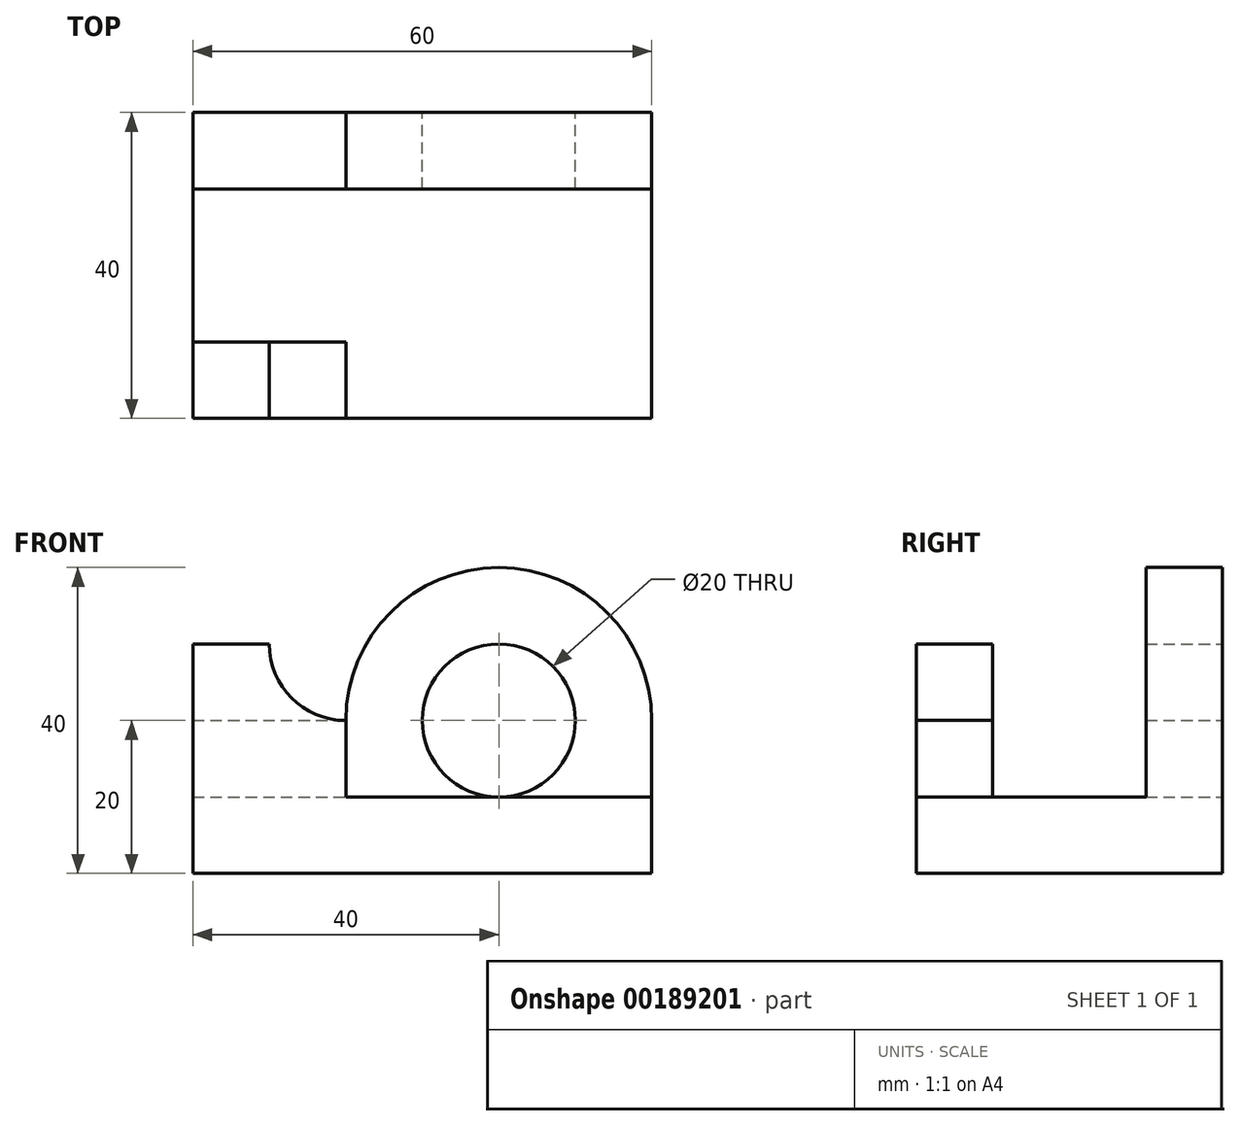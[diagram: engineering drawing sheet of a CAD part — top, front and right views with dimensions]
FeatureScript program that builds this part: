
annotation { "Feature Type Name" : "Feature", "Feature Type Description" : "" }
export const myFeature = defineFeature(function(context is Context, id is Id, definition is map)
    precondition{}
    {
        {
            var Q0;
            Q0=qCreatedBy(makeId("Top.planeOp"),FACE);
            var sketch = newSketch(context, id + "F0", { "sketchPlane" : qUnion([Q0])});
            skLineSegment(sketch, "E0.bottom", {"start": v(0, 0) * mm, "end": v(60, 0) * mm});
            skLineSegment(sketch, "E0.top", {"start": v(0, 40) * mm, "end": v(60, 40) * mm});
            skLineSegment(sketch, "E0.left", {"start": v(0, 0) * mm, "end": v(0, 40) * mm});
            skLineSegment(sketch, "E0.right", {"start": v(60, 0) * mm, "end": v(60, 40) * mm});
            skSolve(sketch);
        }
        {
            var Q0;
            Q0=makeQuery(id+"F0.imprint","IMPRINT",FACE,{"disambiguationData":[TD([[makeQuery(id+"F0.imprint","IMPRINT",EDGE,{"derivedFrom":sQuery(id+"F0.wireOp",EDGE,"E0.bottom")}),1.0]])]});
            extrude(context, id + "F1", {"entities" : qUnion([Q0]), "depth" : 10 * mm});
        }
        {
            var Q0;
            Q0=makeQuery(id+"F1.opExtrude","SWEPT_FACE",FACE,{"disambiguationData":[OSD([sQuery(id+"F0.wireOp",EDGE,"E0.bottom")])]});
            var sketch = newSketch(context, id + "F2", { "sketchPlane" : qUnion([Q0])});
            skLineSegment(sketch, "E1", {"start": v(0, 10) * mm, "end": v(0, 30) * mm});
            skLineSegment(sketch, "E2", {"start": v(0, 30) * mm, "end": v(10, 30) * mm});
            skLineSegment(sketch, "E3", {"start": v(0, 10) * mm, "end": v(20, 10) * mm});
            skLineSegment(sketch, "E4", {"start": v(20, 10) * mm, "end": v(20, 20) * mm});
            skArc(sketch, "E5", {"start": v(10, 30) * mm, "mid": v(12.93, 22.93) * mm, "end": v(20, 20) * mm});
            skSolve(sketch);
        }
        {
            var Q0;
            Q0=makeQuery(id+"F2.imprint","IMPRINT",FACE,{"disambiguationData":[TD([[makeQuery(id+"F2.imprint","IMPRINT",EDGE,{"derivedFrom":sQuery(id+"F2.wireOp",EDGE,"E1")}),-1.0]])]});
            extrude(context, id + "F3", {"entities" : qUnion([Q0]), "operationType" : NewBodyOperationType.ADD, "oppositeDirection" : true, "depth" : 10 * mm});
        }
        {
            var Q0;
            Q0=makeQuery(id+"F1.opExtrude","SWEPT_FACE",FACE,{"disambiguationData":[OSD([sQuery(id+"F0.wireOp",EDGE,"E0.top")])]});
            var sketch = newSketch(context, id + "F4", { "sketchPlane" : qUnion([Q0])});
            skLineSegment(sketch, "E6.0", {"start": v(0, 10) * mm, "end": v(-60, 10) * mm});
            skLineSegment(sketch, "E7", {"start": v(-60, 10) * mm, "end": v(-60, 20) * mm});
            skLineSegment(sketch, "E8", {"start": v(0, 10) * mm, "end": v(0, 20) * mm});
            skArc(sketch, "E9", {"start": v(-20, 20) * mm, "mid": v(-40, 40) * mm, "end": v(-60, 20) * mm});
            skLineSegment(sketch, "E10", {"start": v(0, 20) * mm, "end": v(-20, 20) * mm});
            skSolve(sketch);
        }
        {
            var Q0;
            {var subQ1=sQuery(id+"F4.wireOp",EDGE,"E7");Q0=makeQuery(id+"F4.imprint","IMPRINT",FACE,{"disambiguationData":[TD([[makeQuery(id+"F4.imprint","IMPRINT",EDGE,{"derivedFrom":subQ1}),-1.0]])]});}
            extrude(context, id + "F5", {"entities" : qUnion([Q0]), "operationType" : NewBodyOperationType.ADD, "oppositeDirection" : true, "depth" : 10 * mm});
        }
        {
            var Q0;
            Q0=makeQuery(id+"F4.imprint","IMPRINT",FACE,{"disambiguationData":[TD([[makeQuery(id+"F4.imprint","IMPRINT",EDGE,{"derivedFrom":sQuery(id+"F4.wireOp",EDGE,"E6.0")}),-1.0]])]});
            var sketch = newSketch(context, id + "F6", { "sketchPlane" : qUnion([Q0])});
            skCircle(sketch, "E11", {"center": v(-40, 20) * mm, "radius": 10 * mm});
            skSolve(sketch);
        }
        {
            var Q0;
            Q0=makeQuery(id+"F6.imprint","IMPRINT",FACE,{"disambiguationData":[TD([[makeQuery(id+"F6.imprint","IMPRINT",EDGE,{"derivedFrom":sQuery(id+"F6.wireOp",EDGE,"E11")}),1.0]])]});
            extrude(context, id + "F7", {"entities" : qUnion([Q0]), "operationType" : NewBodyOperationType.REMOVE, "oppositeDirection" : true, "depth" : 25 * mm});
        }
    });
